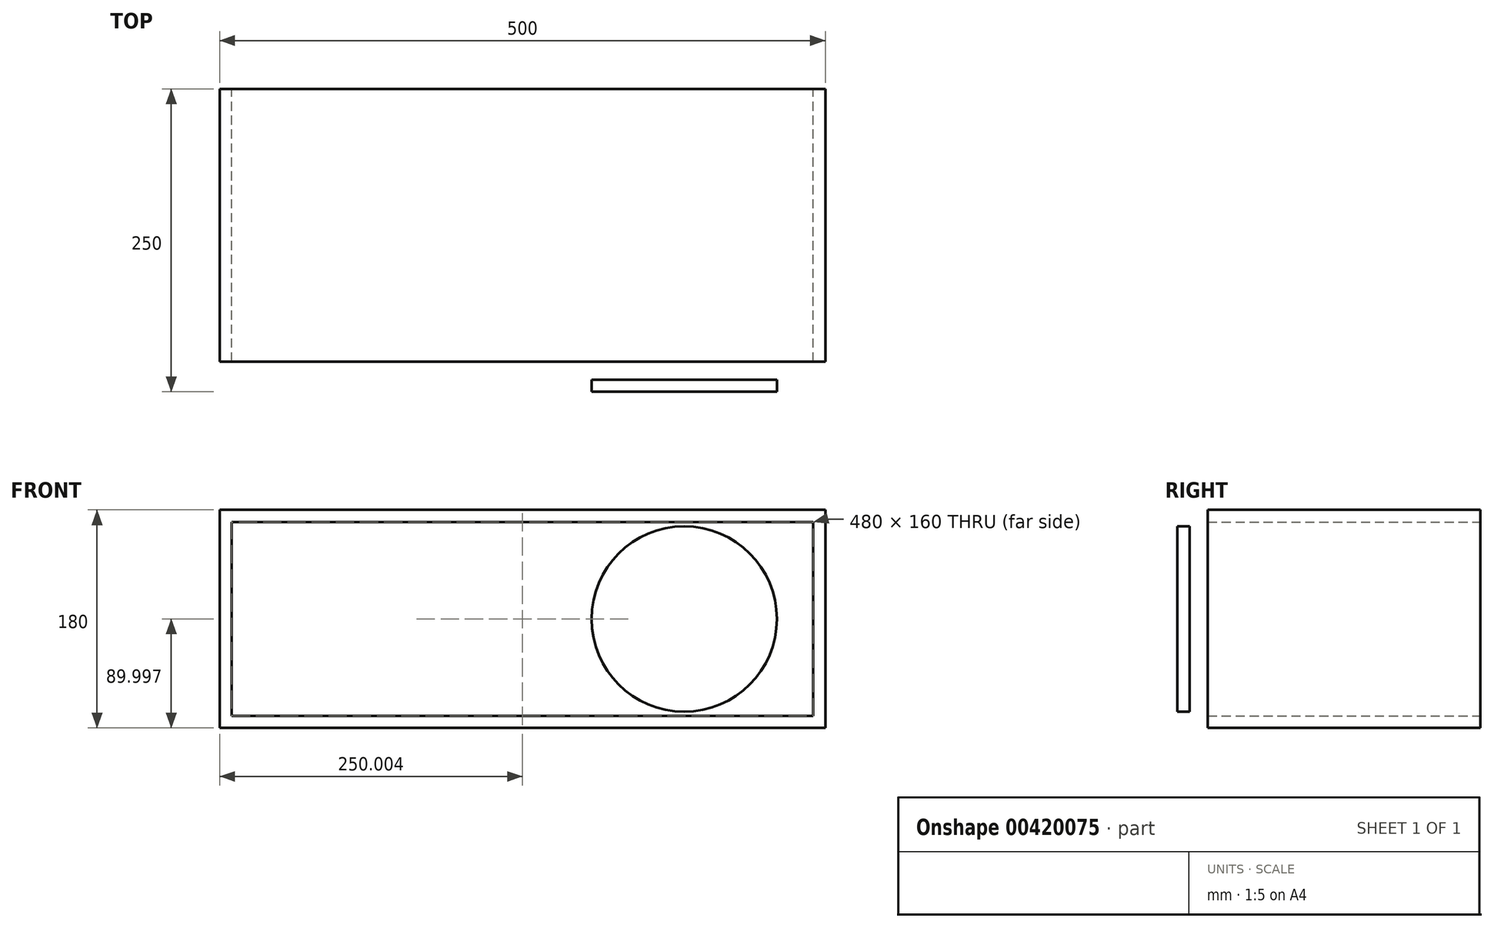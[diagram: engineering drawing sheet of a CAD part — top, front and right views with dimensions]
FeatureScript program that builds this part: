
annotation { "Feature Type Name" : "Feature", "Feature Type Description" : "" }
export const myFeature = defineFeature(function(context is Context, id is Id, definition is map)
    precondition{}
    {
        {
            var Q0;
            Q0=qCreatedBy(makeId("Front.planeOp"),FACE);
            var sketch = newSketch(context, id + "F0", { "sketchPlane" : qUnion([Q0])});
            skLineSegment(sketch, "E0.bottom", {"start": v(-233.37, 86.26) * mm, "end": v(266.63, 86.26) * mm});
            skLineSegment(sketch, "E0.top", {"start": v(-233.37, -93.74) * mm, "end": v(266.63, -93.74) * mm});
            skLineSegment(sketch, "E0.left", {"start": v(-233.37, 86.26) * mm, "end": v(-233.37, -93.74) * mm});
            skLineSegment(sketch, "E0.right", {"start": v(266.63, 86.26) * mm, "end": v(266.63, -93.74) * mm});
            skSolve(sketch);
        }
        {
            var Q0;
            Q0=makeQuery(id+"F0.imprint","IMPRINT",FACE,{"disambiguationData":[TD([[makeQuery(id+"F0.imprint","IMPRINT",EDGE,{"derivedFrom":sQuery(id+"F0.wireOp",EDGE,"E0.bottom")}),-1.0]])]});
            extrude(context, id + "F1", {"entities" : qUnion([Q0]), "depth" : 250 * mm});
        }
        {
            var Q0;
            Q0=makeQuery(id+"F1.opExtrude","CAP_FACE",FACE,{"disambiguationData":[OSD([sQuery(id+"F0.wireOp",EDGE,"E0.bottom"),sQuery(id+"F0.wireOp",EDGE,"E0.top"),sQuery(id+"F0.wireOp",EDGE,"E0.left"),sQuery(id+"F0.wireOp",EDGE,"E0.right")])],"isStart":true});
            shell(context, id + "F2", {"entities" : qUnion([Q0]), "thickness" : 10 * mm});
        }
        {
            var Q0;
            Q0=makeQuery(id+"F1.opExtrude","CAP_FACE",FACE,{"disambiguationData":[OSD([sQuery(id+"F0.wireOp",EDGE,"E0.bottom"),sQuery(id+"F0.wireOp",EDGE,"E0.top"),sQuery(id+"F0.wireOp",EDGE,"E0.left"),sQuery(id+"F0.wireOp",EDGE,"E0.right")])],"isStart":false});
            var sketch = newSketch(context, id + "F3", { "sketchPlane" : qUnion([Q0])});
            skCircle(sketch, "E1", {"center": v(-116.87, -3.74) * mm, "radius": 76.5 * mm});
            skLineSegment(sketch, "E2", {"start": v(16.63, 19.64) * mm, "end": v(16.63, -43.09) * mm});
            skCircle(sketch, "E3.MirrorC", {"center": v(150.13, -3.74) * mm, "radius": 76.5 * mm});
            skSolve(sketch);
        }
        {
            var Q0;
            Q0=makeQuery(id+"F3.imprint","IMPRINT",FACE,{"disambiguationData":[TD([[makeQuery(id+"F3.imprint","IMPRINT",EDGE,{"derivedFrom":sQuery(id+"F3.wireOp",EDGE,"E1")}),1.0]])]});
            var Q1;
            Q1=makeQuery(id+"F3.imprint","IMPRINT",FACE,{"disambiguationData":[TD([[makeQuery(id+"F3.imprint","IMPRINT",EDGE,{"derivedFrom":sQuery(id+"F3.wireOp",EDGE,"E3.MirrorC")}),-1.0]])]});
            extrude(context, id + "F4", {"entities" : qUnion([Q0, Q1]), "operationType" : NewBodyOperationType.REMOVE, "oppositeDirection" : true, "depth" : 25 * mm});
        }
    });
